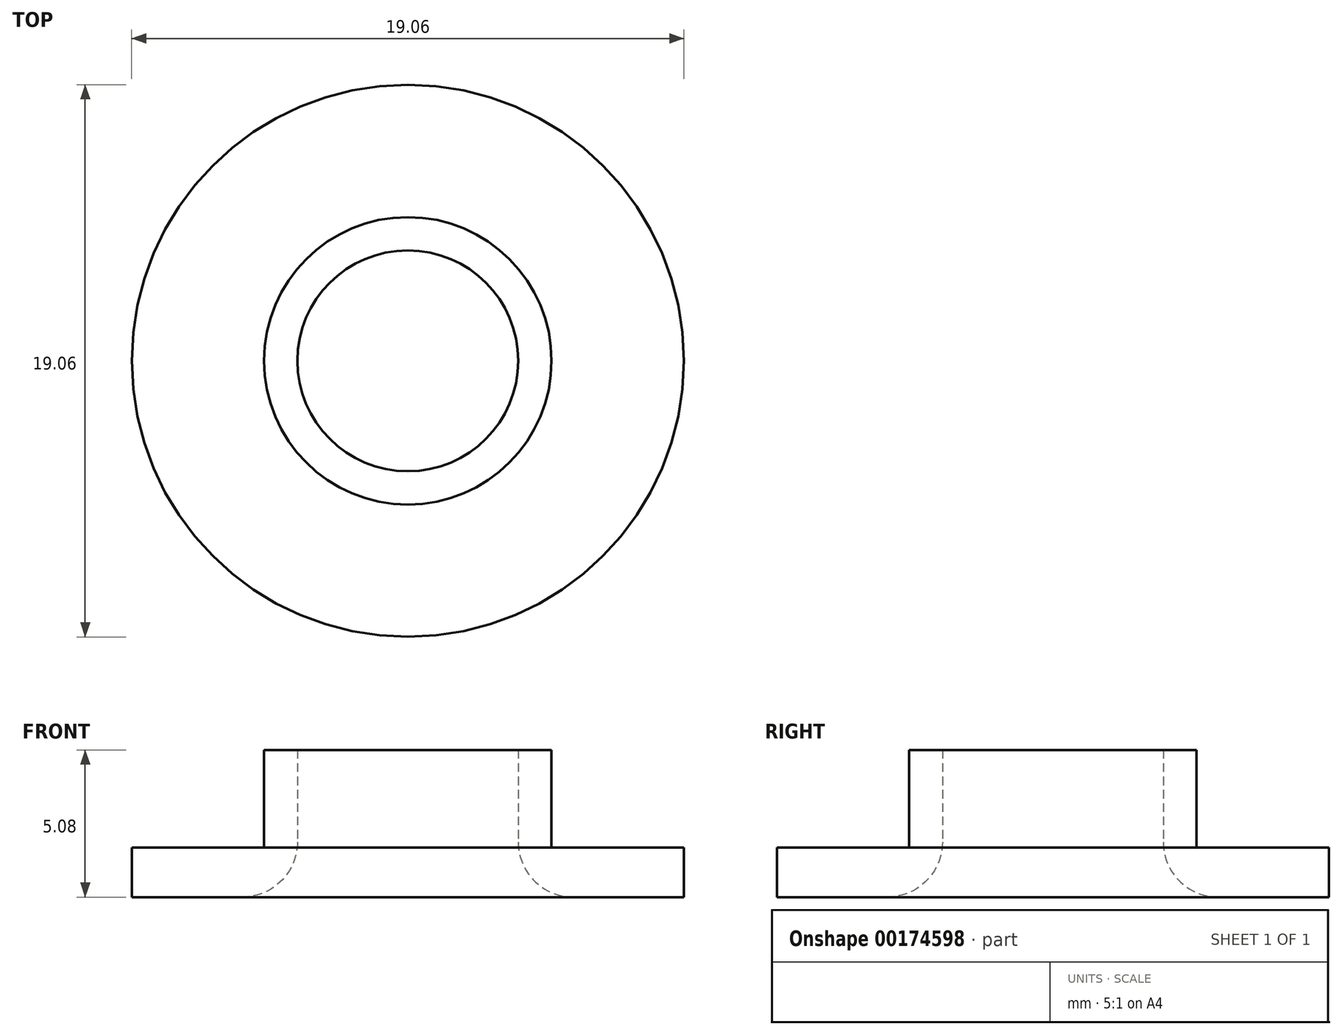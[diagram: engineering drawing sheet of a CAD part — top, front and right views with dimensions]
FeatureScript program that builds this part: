
annotation { "Feature Type Name" : "Feature", "Feature Type Description" : "" }
export const myFeature = defineFeature(function(context is Context, id is Id, definition is map)
    precondition{}
    {
        {
            var Q0;
            Q0=qCreatedBy(makeId("Top.planeOp"),FACE);
            var sketch = newSketch(context, id + "F0", { "sketchPlane" : qUnion([Q0])});
            skCircle(sketch, "E0", {"center": v(0, 0) * mm, "radius": 9.53 * mm});
            skCircle(sketch, "E1", {"center": v(0, 0) * mm, "radius": 4.96 * mm});
            skCircle(sketch, "E2", {"center": v(0, 0) * mm, "radius": 3.81 * mm});
            skSolve(sketch);
        }
        {
            var Q0;
            Q0=makeQuery(id+"F0.imprint","IMPRINT",FACE,{"disambiguationData":[TD([[makeQuery(id+"F0.imprint","IMPRINT",EDGE,{"derivedFrom":sQuery(id+"F0.wireOp",EDGE,"E0")}),1.0]])]});
            extrude(context, id + "F1", {"entities" : qUnion([Q0]), "depth" : 1.71 * mm});
        }
        {
            var Q0;
            Q0=makeQuery(id+"F0.imprint","IMPRINT",FACE,{"disambiguationData":[TD([[makeQuery(id+"F0.imprint","IMPRINT",EDGE,{"derivedFrom":sQuery(id+"F0.wireOp",EDGE,"E1")}),1.0]])]});
            extrude(context, id + "F2", {"entities" : qUnion([Q0]), "operationType" : NewBodyOperationType.ADD, "depth" : 5.08 * mm});
        }
        {
            var Q0;
            Q0=makeQuery(id+"F2.opExtrude","CAP_EDGE",EDGE,{"disambiguationData":[OSD([sQuery(id+"F0.wireOp",EDGE,"E2")])],"isStart":true});
            fillet(context, id + "F3", {"entities" : qUnion([Q0]), "radius" : 1.9 * mm, "tangentPropagation" : true, "allowEdgeOverflow" : false});
        }
    });
